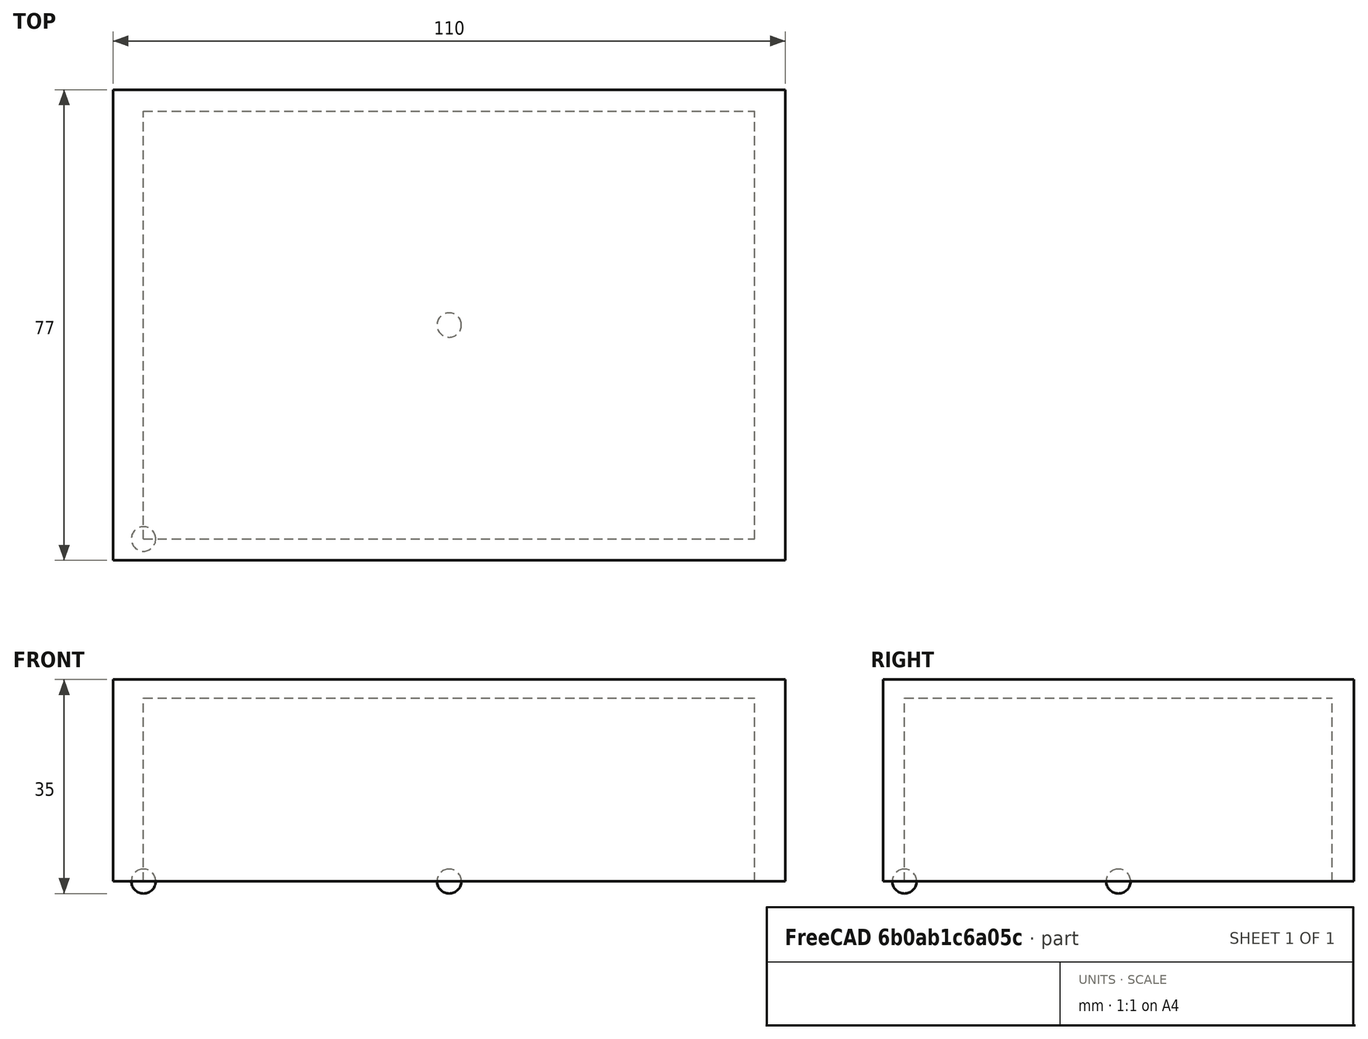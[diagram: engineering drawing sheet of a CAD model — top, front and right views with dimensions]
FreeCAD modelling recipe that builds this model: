
FCSTD DOCUMENT  (FreeCAD 0.14R3700 (Git))
Label: UrsprungMitteAusdehnung
License: CC-BY 3.0
LicenseURL: http://creativecommons.org/licenses/by/3.0/
objects: Part::Box×3, Part::Sphere×2
note: 5 computed .brp shape members not serialized (recipe doc carries the construction recipe); baked Part::Feature solids carry a one-line shape summary decoded from their .brp

FEATURE [Part::Box] Box  label="OriginalObjekt"
  Height = 30
  Length = 100
  Width = 70
FEATURE [Part::Box] Box001  label="ausgedehntObjekt"
  Height = 33
  Length = 110
  Placement = pos=(-5,-3.5,0) rot=(0,0,1;0rad)
  Width = 77
FEATURE [Part::Box] Box002  label="ausgedehntModell"
  Height = 33
  Length = 110
  Placement = pos=(-5,-3.5,0) rot=(0,0,1;0rad)
  Width = 77
FEATURE [Part::Sphere] Sphere  label="Ursprung"
  Angle1 = -90
  Angle2 = 90
  Angle3 = 360
  Placement = pos=(50,35,0) rot=(0,0,1;0rad)
  Radius = 2
FEATURE [Part::Sphere] Sphere001  label="KoordUrsprung"
  Angle1 = -90
  Angle2 = 90
  Angle3 = 360
  Radius = 2
